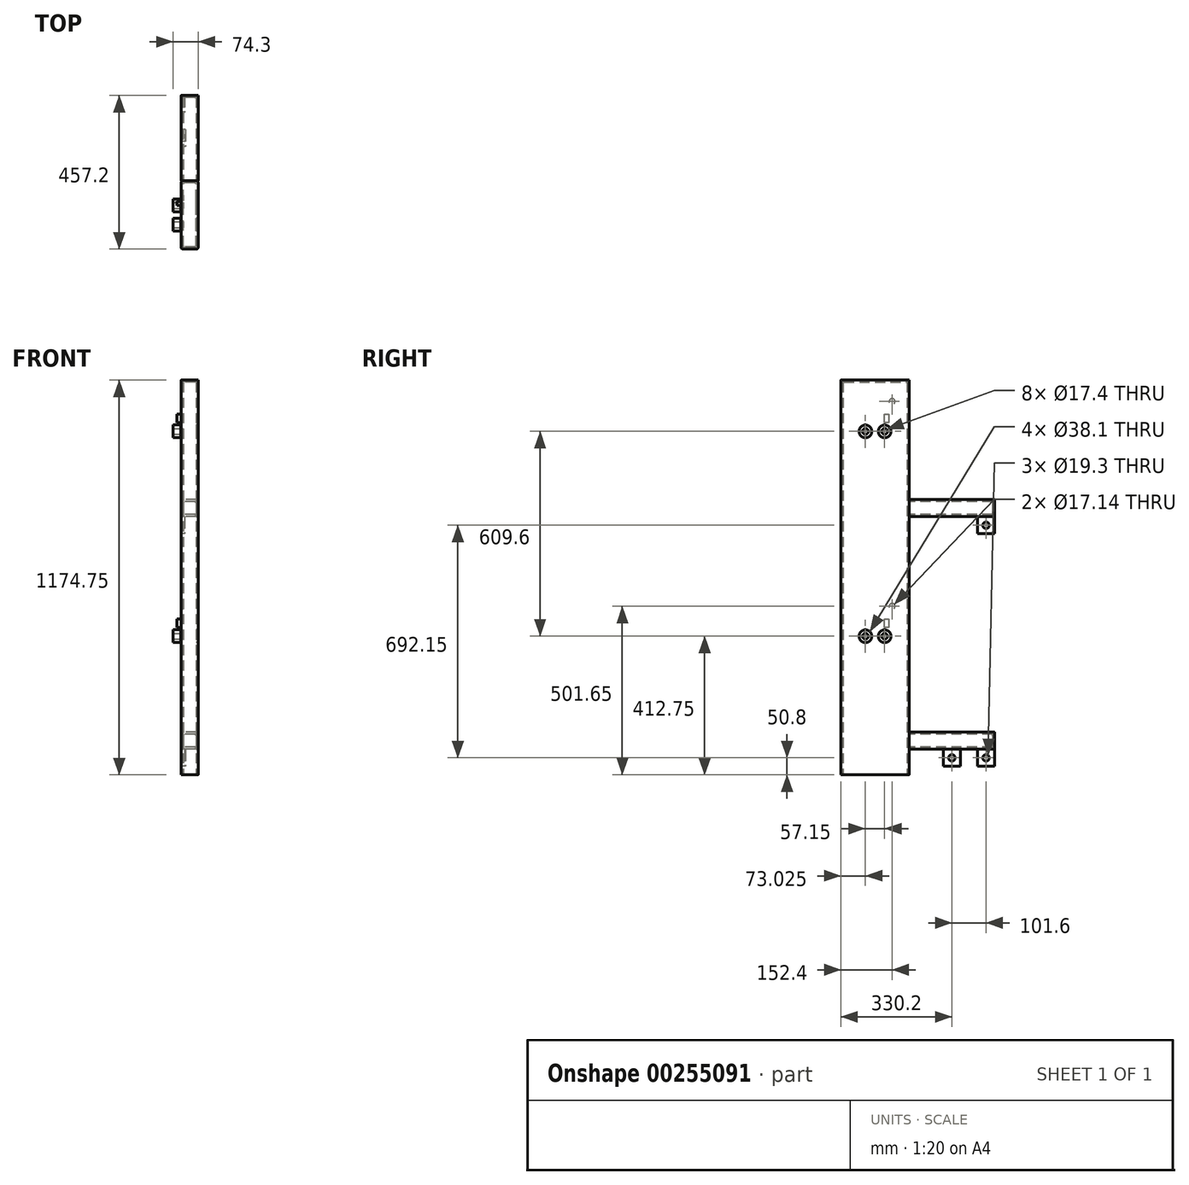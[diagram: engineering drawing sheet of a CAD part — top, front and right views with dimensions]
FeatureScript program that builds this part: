
annotation { "Feature Type Name" : "Feature", "Feature Type Description" : "" }
export const myFeature = defineFeature(function(context is Context, id is Id, definition is map)
    precondition{}
    {
        {
            var Q0;
            Q0=qCreatedBy(makeId("Top.planeOp"),FACE);
            var sketch = newSketch(context, id + "F0", { "sketchPlane" : qUnion([Q0])});
            skLineSegment(sketch, "E0.bottom", {"start": v(19.43, -101.6) * mm, "end": v(-19.43, -101.6) * mm});
            skLineSegment(sketch, "E0.top", {"start": v(19.43, 101.6) * mm, "end": v(-19.43, 101.6) * mm});
            skLineSegment(sketch, "E0.left", {"start": v(25.4, -95.63) * mm, "end": v(25.4, 95.63) * mm});
            skLineSegment(sketch, "E0.right", {"start": v(-25.4, -95.63) * mm, "end": v(-25.4, 95.63) * mm});
            skPoint(sketch, "E0.middle", {"position": v(0, 0) * mm});
            skLineSegment(sketch, "E1.0", {"start": v(-19.05, -92.08) * mm, "end": v(-19.05, 92.08) * mm});
            skLineSegment(sketch, "E1.1", {"start": v(15.87, -95.25) * mm, "end": v(-15.88, -95.25) * mm});
            skLineSegment(sketch, "E1.2", {"start": v(19.05, -92.08) * mm, "end": v(19.05, 92.08) * mm});
            skLineSegment(sketch, "E1.3", {"start": v(15.88, 95.25) * mm, "end": v(-15.88, 95.25) * mm});
            skPoint(sketch, "E2.visualSharp", {"position": v(-19.05, 95.25) * mm});
            skArc(sketch, "E2.filletArc", {"start": v(-15.88, 95.25) * mm, "mid": v(-18.12, 94.32) * mm, "end": v(-19.05, 92.08) * mm});
            skPoint(sketch, "E3.visualSharp", {"position": v(19.05, 95.25) * mm});
            skArc(sketch, "E3.filletArc", {"start": v(19.05, 92.08) * mm, "mid": v(18.12, 94.32) * mm, "end": v(15.88, 95.25) * mm});
            skPoint(sketch, "E4.visualSharp", {"position": v(19.05, -95.25) * mm});
            skArc(sketch, "E4.filletArc", {"start": v(15.87, -95.25) * mm, "mid": v(18.12, -94.32) * mm, "end": v(19.05, -92.08) * mm});
            skPoint(sketch, "E5.visualSharp", {"position": v(-19.05, -95.25) * mm});
            skArc(sketch, "E5.filletArc", {"start": v(-19.05, -92.08) * mm, "mid": v(-18.12, -94.32) * mm, "end": v(-15.88, -95.25) * mm});
            skPoint(sketch, "E6.visualSharp", {"position": v(-25.4, 101.6) * mm});
            skArc(sketch, "E6.filletArc", {"start": v(-19.43, 101.6) * mm, "mid": v(-23.65, 99.85) * mm, "end": v(-25.4, 95.63) * mm});
            skPoint(sketch, "E7.visualSharp", {"position": v(25.4, 101.6) * mm});
            skArc(sketch, "E7.filletArc", {"start": v(25.4, 95.63) * mm, "mid": v(23.65, 99.85) * mm, "end": v(19.43, 101.6) * mm});
            skPoint(sketch, "E8.visualSharp", {"position": v(25.4, -101.6) * mm});
            skArc(sketch, "E8.filletArc", {"start": v(19.43, -101.6) * mm, "mid": v(23.65, -99.85) * mm, "end": v(25.4, -95.63) * mm});
            skPoint(sketch, "E9.visualSharp", {"position": v(-25.4, -101.6) * mm});
            skArc(sketch, "E9.filletArc", {"start": v(-25.4, -95.63) * mm, "mid": v(-23.65, -99.85) * mm, "end": v(-19.43, -101.6) * mm});
            skSolve(sketch);
        }
        {
            var Q0;
            Q0 = qSketchRegion(id + "F0", true);
            extrude(context, id + "F1", {"entities" : qUnion([Q0]), "depth" : 1168.4 * mm});
        }
        {
            var Q0;
            Q0=makeQuery(id+"F1.opExtrude","CAP_FACE",FACE,{"disambiguationData":[OSD([sQuery(id+"F0.wireOp",EDGE,"E0.bottom"),sQuery(id+"F0.wireOp",EDGE,"E0.top"),sQuery(id+"F0.wireOp",EDGE,"E0.left"),sQuery(id+"F0.wireOp",EDGE,"E0.right"),sQuery(id+"F0.wireOp",EDGE,"E1.0"),sQuery(id+"F0.wireOp",EDGE,"E1.1"),sQuery(id+"F0.wireOp",EDGE,"E1.2"),sQuery(id+"F0.wireOp",EDGE,"E1.3"),sQuery(id+"F0.wireOp",EDGE,"E2.filletArc"),sQuery(id+"F0.wireOp",EDGE,"E3.filletArc"),sQuery(id+"F0.wireOp",EDGE,"E4.filletArc"),sQuery(id+"F0.wireOp",EDGE,"E5.filletArc"),sQuery(id+"F0.wireOp",EDGE,"E6.filletArc"),sQuery(id+"F0.wireOp",EDGE,"E7.filletArc"),sQuery(id+"F0.wireOp",EDGE,"E8.filletArc"),sQuery(id+"F0.wireOp",EDGE,"E9.filletArc")])],"isStart":false});
            var sketch = newSketch(context, id + "F2", { "sketchPlane" : qUnion([Q0])});
            skArc(sketch, "E10.0", {"start": v(-19.43, 101.6) * mm, "mid": v(-23.65, 99.85) * mm, "end": v(-25.4, 95.63) * mm});
            skLineSegment(sketch, "E10.1", {"start": v(19.43, 101.6) * mm, "end": v(-19.43, 101.6) * mm});
            skArc(sketch, "E10.2", {"start": v(25.4, 95.63) * mm, "mid": v(23.65, 99.85) * mm, "end": v(19.43, 101.6) * mm});
            skLineSegment(sketch, "E10.3", {"start": v(25.4, -95.63) * mm, "end": v(25.4, 95.63) * mm});
            skLineSegment(sketch, "E10.4", {"start": v(-25.4, -95.63) * mm, "end": v(-25.4, 95.63) * mm});
            skArc(sketch, "E10.5", {"start": v(-25.4, -95.63) * mm, "mid": v(-23.65, -99.85) * mm, "end": v(-19.43, -101.6) * mm});
            skLineSegment(sketch, "E10.6", {"start": v(19.43, -101.6) * mm, "end": v(-19.43, -101.6) * mm});
            skArc(sketch, "E10.7", {"start": v(19.43, -101.6) * mm, "mid": v(23.65, -99.85) * mm, "end": v(25.4, -95.63) * mm});
            skSolve(sketch);
        }
        {
            var Q0;
            Q0 = qSketchRegion(id + "F2", true);
            extrude(context, id + "F3", {"entities" : qUnion([Q0]), "operationType" : NewBodyOperationType.ADD, "depth" : 6.35 * mm});
        }
        {
            var Q0;
            Q0=makeQuery(id+"F3.boolean.opBoolean","MERGE",FACE,{"derivedFrom":[makeQuery(id+"F1.opExtrude","SWEPT_FACE",FACE,{"disambiguationData":[OSD([sQuery(id+"F0.wireOp",EDGE,"E0.right")])]}),makeQuery(id+"F3.opExtrude","SWEPT_FACE",FACE,{"disambiguationData":[OSD([sQuery(id+"F2.wireOp",EDGE,"E10.4")])]})]});
            var sketch = newSketch(context, id + "F4", { "sketchPlane" : qUnion([Q0])});
            skLineSegment(sketch, "E11", {"start": v(-119.84, 1022.35) * mm, "end": v(114.78, 1022.35) * mm, "construction": true});
            skLineSegment(sketch, "E12", {"start": v(0, 1307.78) * mm, "end": v(0, -150.73) * mm, "construction": true});
            skPoint(sketch, "E13.orphan", {"position": v(0, 1174.75) * mm});
            skCircle(sketch, "E14", {"center": v(28.57, 1022.35) * mm, "radius": 19.05 * mm});
            skCircle(sketch, "E15", {"center": v(-28.58, 1022.35) * mm, "radius": 19.05 * mm});
            skCircle(sketch, "E16.0.1.0", {"center": v(-28.58, 412.75) * mm, "radius": 19.05 * mm});
            skCircle(sketch, "E16.0.1.1", {"center": v(28.57, 412.75) * mm, "radius": 19.05 * mm});
            skLineSegment(sketch, "E16.direction1", {"start": v(-28.58, 1022.35) * mm, "end": v(-3.18, 1022.35) * mm, "construction": true});
            skLineSegment(sketch, "E16.direction2", {"start": v(-28.58, 1022.35) * mm, "end": v(-28.58, 412.75) * mm, "construction": true});
            skSolve(sketch);
        }
        {
            var Q0;
            Q0 = qSketchRegion(id + "F4", true);
            extrude(context, id + "F5", {"entities" : qUnion([Q0]), "depth" : 23.5 * mm, "hasSecondDirection" : true, "secondDirectionOppositeDirection" : false, "secondDirectionDepth" : 1.27 * mm});
        }
        {
            var Q0;
            Q0=makeQuery(id+"F5.opExtrude","CAP_FACE",FACE,{"disambiguationData":[OSD([sQuery(id+"F4.wireOp",EDGE,"E14")])],"isStart":true});
            var sketch = newSketch(context, id + "F6", { "sketchPlane" : qUnion([Q0])});
            skCircle(sketch, "E17", {"center": v(-28.57, 1022.35) * mm, "radius": 7.94 * mm});
            skCircle(sketch, "E18", {"center": v(-28.57, 412.75) * mm, "radius": 7.94 * mm});
            skLineSegment(sketch, "E19", {"start": v(-28.57, 1075.13) * mm, "end": v(-28.57, 568.16) * mm, "construction": true});
            skSolve(sketch);
        }
        {
            var Q0;
            Q0 = qSketchRegion(id + "F6", true);
            extrude(context, id + "F7", {"entities" : qUnion([Q0]), "operationType" : NewBodyOperationType.ADD, "depth" : 38.1 * mm});
        }
        {
            var Q0;
            Q0=makeQuery(id+"F5.opExtrude","CAP_FACE",FACE,{"disambiguationData":[OSD([sQuery(id+"F4.wireOp",EDGE,"E15")])],"isStart":true});
            var sketch = newSketch(context, id + "F8", { "sketchPlane" : qUnion([Q0])});
            skCircle(sketch, "E20", {"center": v(28.58, 1022.35) * mm, "radius": 7.94 * mm});
            skLineSegment(sketch, "E21", {"start": v(28.58, 1064.46) * mm, "end": v(28.58, 607.48) * mm, "construction": true});
            skCircle(sketch, "E22", {"center": v(28.58, 412.75) * mm, "radius": 7.94 * mm});
            skSolve(sketch);
        }
        {
            var Q0;
            Q0 = qSketchRegion(id + "F8", true);
            extrude(context, id + "F9", {"entities" : qUnion([Q0]), "operationType" : NewBodyOperationType.ADD, "depth" : 38.1 * mm});
        }
        {
            var Q0;
            Q0=makeQuery(id+"F7.opExtrude","CAP_FACE",FACE,{"disambiguationData":[OSD([sQuery(id+"F6.wireOp",EDGE,"E17")])],"isStart":false});
            var sketch = newSketch(context, id + "F10", { "sketchPlane" : qUnion([Q0])});
            skCircle(sketch, "E23", {"center": v(-28.57, 1022.35) * mm, "radius": 19.05 * mm});
            skCircle(sketch, "E24", {"center": v(28.58, 1022.35) * mm, "radius": 19.05 * mm});
            skCircle(sketch, "E25.0.1.0", {"center": v(-28.57, 412.75) * mm, "radius": 19.05 * mm});
            skCircle(sketch, "E25.0.1.1", {"center": v(28.58, 412.75) * mm, "radius": 19.05 * mm});
            skLineSegment(sketch, "E25.direction1", {"start": v(-28.57, 1022.35) * mm, "end": v(-3.17, 1022.35) * mm, "construction": true});
            skLineSegment(sketch, "E25.direction2", {"start": v(-28.57, 1022.35) * mm, "end": v(-28.57, 412.75) * mm, "construction": true});
            skSolve(sketch);
        }
        {
            var Q0;
            Q0 = qSketchRegion(id + "F10", true);
            var Q1;
            Q1=makeQuery(id+"F3.boolean.opBoolean","MERGE",FACE,{"derivedFrom":[makeQuery(id+"F1.opExtrude","SWEPT_FACE",FACE,{"disambiguationData":[OSD([sQuery(id+"F0.wireOp",EDGE,"E0.left")])]}),makeQuery(id+"F3.opExtrude","SWEPT_FACE",FACE,{"disambiguationData":[OSD([sQuery(id+"F2.wireOp",EDGE,"E10.3")])]})]});
            extrude(context, id + "F11", {"entities" : qUnion([Q0]), "operationType" : NewBodyOperationType.REMOVE, "endBound" : BoundingType.UP_TO_SURFACE, "endBoundEntityFace" : qUnion([Q1]), "depth" : 25.4 * mm});
        }
        {
            var Q0;
            Q0=makeQuery(id+"F3.boolean.opBoolean","MERGE",FACE,{"derivedFrom":[makeQuery(id+"F1.opExtrude","SWEPT_FACE",FACE,{"disambiguationData":[OSD([sQuery(id+"F0.wireOp",EDGE,"E0.right")])]}),makeQuery(id+"F3.opExtrude","SWEPT_FACE",FACE,{"disambiguationData":[OSD([sQuery(id+"F2.wireOp",EDGE,"E10.4")])]})]});
            var sketch = newSketch(context, id + "F12", { "sketchPlane" : qUnion([Q0])});
            skLineSegment(sketch, "E26", {"start": v(-28.58, 1047.75) * mm, "end": v(-28.58, 1073.15) * mm});
            skLineSegment(sketch, "E27", {"start": v(-28.58, 1073.15) * mm, "end": v(-41.28, 1073.15) * mm});
            skLineSegment(sketch, "E28", {"start": v(-41.28, 1073.15) * mm, "end": v(-41.28, 1047.75) * mm});
            skLineSegment(sketch, "E29", {"start": v(-41.28, 1047.75) * mm, "end": v(-28.58, 1047.75) * mm});
            skLineSegment(sketch, "E30", {"start": v(-79.96, 1022.35) * mm, "end": v(86.7, 1022.35) * mm, "construction": true});
            skPoint(sketch, "E31", {"position": v(-28.58, 1022.35) * mm});
            skLineSegment(sketch, "E32.0.1.0", {"start": v(-41.28, 463.55) * mm, "end": v(-41.28, 438.15) * mm});
            skLineSegment(sketch, "E32.0.1.1", {"start": v(-28.58, 463.55) * mm, "end": v(-41.28, 463.55) * mm});
            skLineSegment(sketch, "E32.0.1.2", {"start": v(-28.58, 438.15) * mm, "end": v(-28.58, 463.55) * mm});
            skLineSegment(sketch, "E32.0.1.3", {"start": v(-41.28, 438.15) * mm, "end": v(-28.58, 438.15) * mm});
            skLineSegment(sketch, "E32.direction1", {"start": v(-41.28, 1047.75) * mm, "end": v(-15.88, 1047.75) * mm, "construction": true});
            skLineSegment(sketch, "E32.direction2", {"start": v(-41.28, 1047.75) * mm, "end": v(-41.28, 438.15) * mm, "construction": true});
            skSolve(sketch);
        }
        {
            var Q0;
            Q0 = qSketchRegion(id + "F12", true);
            extrude(context, id + "F13", {"entities" : qUnion([Q0]), "operationType" : NewBodyOperationType.ADD, "depth" : 12.7 * mm});
        }
        {
            var Q0;
            Q0=makeQuery(id+"F3.boolean.opBoolean","MERGE",FACE,{"derivedFrom":[makeQuery(id+"F1.opExtrude","SWEPT_FACE",FACE,{"disambiguationData":[OSD([sQuery(id+"F0.wireOp",EDGE,"E0.left")])]}),makeQuery(id+"F3.opExtrude","SWEPT_FACE",FACE,{"disambiguationData":[OSD([sQuery(id+"F2.wireOp",EDGE,"E10.3")])]})]});
            var sketch = newSketch(context, id + "F14", { "sketchPlane" : qUnion([Q0])});
            skCircle(sketch, "E33", {"center": v(-28.57, 1022.35) * mm, "radius": 8.7 * mm});
            skCircle(sketch, "E34", {"center": v(28.58, 1022.35) * mm, "radius": 8.7 * mm});
            skCircle(sketch, "E35.0.1.0", {"center": v(28.58, 412.75) * mm, "radius": 8.7 * mm});
            skCircle(sketch, "E35.0.1.1", {"center": v(-28.57, 412.75) * mm, "radius": 8.7 * mm});
            skLineSegment(sketch, "E35.direction1", {"start": v(-28.57, 1022.35) * mm, "end": v(-3.17, 1022.35) * mm, "construction": true});
            skLineSegment(sketch, "E35.direction2", {"start": v(-28.57, 1022.35) * mm, "end": v(-28.57, 412.75) * mm, "construction": true});
            skSolve(sketch);
        }
        {
            var Q0;
            Q0 = qSketchRegion(id + "F14", true);
            extrude(context, id + "F15", {"entities" : qUnion([Q0]), "operationType" : NewBodyOperationType.REMOVE, "endBound" : BoundingType.THROUGH_ALL, "oppositeDirection" : true, "depth" : 25.4 * mm});
        }
        {
            var Q0;
            Q0=makeQuery(id+"F3.boolean.opBoolean","MERGE",FACE,{"derivedFrom":[makeQuery(id+"F1.opExtrude","SWEPT_FACE",FACE,{"disambiguationData":[OSD([sQuery(id+"F0.wireOp",EDGE,"E0.top")])]}),makeQuery(id+"F3.opExtrude","SWEPT_FACE",FACE,{"disambiguationData":[OSD([sQuery(id+"F2.wireOp",EDGE,"E10.1")])]})]});
            var sketch = newSketch(context, id + "F16", { "sketchPlane" : qUnion([Q0])});
            skLineSegment(sketch, "E36.bottom", {"start": v(-19.43, 819.15) * mm, "end": v(19.43, 819.15) * mm});
            skLineSegment(sketch, "E36.top", {"start": v(-19.43, 768.35) * mm, "end": v(19.43, 768.35) * mm});
            skLineSegment(sketch, "E36.left", {"start": v(-25.4, 813.18) * mm, "end": v(-25.4, 774.32) * mm});
            skLineSegment(sketch, "E36.right", {"start": v(25.4, 813.18) * mm, "end": v(25.4, 774.32) * mm});
            skLineSegment(sketch, "E37.0", {"start": v(-15.88, 812.8) * mm, "end": v(15.88, 812.8) * mm});
            skLineSegment(sketch, "E37.1", {"start": v(-19.05, 809.63) * mm, "end": v(-19.05, 777.88) * mm});
            skLineSegment(sketch, "E37.2", {"start": v(-15.88, 774.7) * mm, "end": v(15.88, 774.7) * mm});
            skLineSegment(sketch, "E37.3", {"start": v(19.05, 809.63) * mm, "end": v(19.05, 777.88) * mm});
            skPoint(sketch, "E38.visualSharp", {"position": v(19.05, 812.8) * mm});
            skArc(sketch, "E38.filletArc", {"start": v(19.05, 809.63) * mm, "mid": v(18.12, 811.87) * mm, "end": v(15.88, 812.8) * mm});
            skPoint(sketch, "E39.visualSharp", {"position": v(19.05, 774.7) * mm});
            skArc(sketch, "E39.filletArc", {"start": v(15.88, 774.7) * mm, "mid": v(18.12, 775.63) * mm, "end": v(19.05, 777.88) * mm});
            skPoint(sketch, "E40.visualSharp", {"position": v(-19.05, 774.7) * mm});
            skArc(sketch, "E40.filletArc", {"start": v(-19.05, 777.88) * mm, "mid": v(-18.12, 775.63) * mm, "end": v(-15.88, 774.7) * mm});
            skPoint(sketch, "E41.visualSharp", {"position": v(-19.05, 812.8) * mm});
            skArc(sketch, "E41.filletArc", {"start": v(-15.88, 812.8) * mm, "mid": v(-18.12, 811.87) * mm, "end": v(-19.05, 809.63) * mm});
            skPoint(sketch, "E42.visualSharp", {"position": v(25.4, 819.15) * mm});
            skArc(sketch, "E42.filletArc", {"start": v(25.4, 813.18) * mm, "mid": v(23.65, 817.4) * mm, "end": v(19.43, 819.15) * mm});
            skPoint(sketch, "E43.visualSharp", {"position": v(25.4, 768.35) * mm});
            skArc(sketch, "E43.filletArc", {"start": v(19.43, 768.35) * mm, "mid": v(23.65, 770.1) * mm, "end": v(25.4, 774.32) * mm});
            skPoint(sketch, "E44.visualSharp", {"position": v(-25.4, 768.35) * mm});
            skArc(sketch, "E44.filletArc", {"start": v(-25.4, 774.32) * mm, "mid": v(-23.65, 770.1) * mm, "end": v(-19.43, 768.35) * mm});
            skPoint(sketch, "E45.visualSharp", {"position": v(-25.4, 819.15) * mm});
            skArc(sketch, "E45.filletArc", {"start": v(-19.43, 819.15) * mm, "mid": v(-23.65, 817.4) * mm, "end": v(-25.4, 813.18) * mm});
            skLineSegment(sketch, "E46.0.1.0", {"start": v(-19.05, 117.48) * mm, "end": v(-19.05, 85.73) * mm});
            skLineSegment(sketch, "E46.0.1.1", {"start": v(-25.4, 121.03) * mm, "end": v(-25.4, 82.17) * mm});
            skLineSegment(sketch, "E46.0.1.2", {"start": v(-15.88, 120.65) * mm, "end": v(15.88, 120.65) * mm});
            skLineSegment(sketch, "E46.0.1.3", {"start": v(19.05, 117.48) * mm, "end": v(19.05, 85.73) * mm});
            skLineSegment(sketch, "E46.0.1.4", {"start": v(-15.88, 82.55) * mm, "end": v(15.88, 82.55) * mm});
            skLineSegment(sketch, "E46.0.1.5", {"start": v(-19.43, 127) * mm, "end": v(19.43, 127) * mm});
            skLineSegment(sketch, "E46.0.1.6", {"start": v(25.4, 121.03) * mm, "end": v(25.4, 82.17) * mm});
            skLineSegment(sketch, "E46.0.1.7", {"start": v(-19.43, 76.2) * mm, "end": v(19.43, 76.2) * mm});
            skArc(sketch, "E46.0.1.8", {"start": v(19.43, 76.2) * mm, "mid": v(23.65, 77.95) * mm, "end": v(25.4, 82.17) * mm});
            skArc(sketch, "E46.0.1.9", {"start": v(-25.4, 82.17) * mm, "mid": v(-23.65, 77.95) * mm, "end": v(-19.43, 76.2) * mm});
            skArc(sketch, "E46.0.1.10", {"start": v(25.4, 121.03) * mm, "mid": v(23.65, 125.25) * mm, "end": v(19.43, 127) * mm});
            skArc(sketch, "E46.0.1.11", {"start": v(-19.43, 127) * mm, "mid": v(-23.65, 125.25) * mm, "end": v(-25.4, 121.03) * mm});
            skArc(sketch, "E46.0.1.12", {"start": v(-15.88, 120.65) * mm, "mid": v(-18.12, 119.72) * mm, "end": v(-19.05, 117.48) * mm});
            skArc(sketch, "E46.0.1.13", {"start": v(-19.05, 85.73) * mm, "mid": v(-18.12, 83.48) * mm, "end": v(-15.88, 82.55) * mm});
            skArc(sketch, "E46.0.1.14", {"start": v(15.88, 82.55) * mm, "mid": v(18.12, 83.48) * mm, "end": v(19.05, 85.73) * mm});
            skArc(sketch, "E46.0.1.15", {"start": v(19.05, 117.48) * mm, "mid": v(18.12, 119.72) * mm, "end": v(15.88, 120.65) * mm});
            skLineSegment(sketch, "E46.direction1", {"start": v(-19.43, 768.35) * mm, "end": v(5.97, 768.35) * mm, "construction": true});
            skLineSegment(sketch, "E46.direction2", {"start": v(-19.43, 768.35) * mm, "end": v(-19.43, 76.2) * mm, "construction": true});
            skSolve(sketch);
        }
        {
            var Q0;
            Q0 = qSketchRegion(id + "F16", true);
            extrude(context, id + "F17", {"entities" : qUnion([Q0]), "operationType" : NewBodyOperationType.ADD, "depth" : 247.65 * mm});
        }
        {
            var Q0;
            Q0=makeQuery(id+"F17.opExtrude","CAP_FACE",FACE,{"disambiguationData":[OSD([sQuery(id+"F16.wireOp",EDGE,"E36.bottom"),sQuery(id+"F16.wireOp",EDGE,"E36.top"),sQuery(id+"F16.wireOp",EDGE,"E36.left"),sQuery(id+"F16.wireOp",EDGE,"E36.right"),sQuery(id+"F16.wireOp",EDGE,"E37.0"),sQuery(id+"F16.wireOp",EDGE,"E37.1"),sQuery(id+"F16.wireOp",EDGE,"E37.2"),sQuery(id+"F16.wireOp",EDGE,"E37.3"),sQuery(id+"F16.wireOp",EDGE,"E38.filletArc"),sQuery(id+"F16.wireOp",EDGE,"E39.filletArc"),sQuery(id+"F16.wireOp",EDGE,"E40.filletArc"),sQuery(id+"F16.wireOp",EDGE,"E41.filletArc"),sQuery(id+"F16.wireOp",EDGE,"E42.filletArc"),sQuery(id+"F16.wireOp",EDGE,"E43.filletArc"),sQuery(id+"F16.wireOp",EDGE,"E44.filletArc"),sQuery(id+"F16.wireOp",EDGE,"E45.filletArc")])],"isStart":false});
            var sketch = newSketch(context, id + "F18", { "sketchPlane" : qUnion([Q0])});
            skLineSegment(sketch, "E47.0", {"start": v(-19.43, 819.15) * mm, "end": v(19.43, 819.15) * mm});
            skLineSegment(sketch, "E47.1", {"start": v(25.4, 813.18) * mm, "end": v(25.4, 774.32) * mm});
            skLineSegment(sketch, "E47.2", {"start": v(-19.43, 768.35) * mm, "end": v(19.43, 768.35) * mm});
            skLineSegment(sketch, "E47.3", {"start": v(-25.4, 813.18) * mm, "end": v(-25.4, 774.32) * mm});
            skArc(sketch, "E48.0", {"start": v(25.4, 813.18) * mm, "mid": v(23.65, 817.4) * mm, "end": v(19.43, 819.15) * mm});
            skArc(sketch, "E49.0", {"start": v(19.43, 768.35) * mm, "mid": v(23.65, 770.1) * mm, "end": v(25.4, 774.32) * mm});
            skArc(sketch, "E49.1", {"start": v(-25.4, 774.32) * mm, "mid": v(-23.65, 770.1) * mm, "end": v(-19.43, 768.35) * mm});
            skArc(sketch, "E49.2", {"start": v(-19.43, 819.15) * mm, "mid": v(-23.65, 817.4) * mm, "end": v(-25.4, 813.18) * mm});
            skSolve(sketch);
        }
        {
            var Q0;
            Q0 = qSketchRegion(id + "F18", true);
            extrude(context, id + "F19", {"entities" : qUnion([Q0]), "operationType" : NewBodyOperationType.ADD, "depth" : 6.35 * mm});
        }
        {
            var Q0;
            Q0=makeQuery(id+"F17.opExtrude","CAP_FACE",FACE,{"disambiguationData":[OSD([sQuery(id+"F16.wireOp",EDGE,"E46.0.1.0"),sQuery(id+"F16.wireOp",EDGE,"E46.0.1.1"),sQuery(id+"F16.wireOp",EDGE,"E46.0.1.2"),sQuery(id+"F16.wireOp",EDGE,"E46.0.1.3"),sQuery(id+"F16.wireOp",EDGE,"E46.0.1.4"),sQuery(id+"F16.wireOp",EDGE,"E46.0.1.5"),sQuery(id+"F16.wireOp",EDGE,"E46.0.1.6"),sQuery(id+"F16.wireOp",EDGE,"E46.0.1.7"),sQuery(id+"F16.wireOp",EDGE,"E46.0.1.8"),sQuery(id+"F16.wireOp",EDGE,"E46.0.1.9"),sQuery(id+"F16.wireOp",EDGE,"E46.0.1.10"),sQuery(id+"F16.wireOp",EDGE,"E46.0.1.11"),sQuery(id+"F16.wireOp",EDGE,"E46.0.1.12"),sQuery(id+"F16.wireOp",EDGE,"E46.0.1.13"),sQuery(id+"F16.wireOp",EDGE,"E46.0.1.14"),sQuery(id+"F16.wireOp",EDGE,"E46.0.1.15")])],"isStart":false});
            var sketch = newSketch(context, id + "F20", { "sketchPlane" : qUnion([Q0])});
            skLineSegment(sketch, "E50.0", {"start": v(-19.43, 127) * mm, "end": v(19.43, 127) * mm});
            skLineSegment(sketch, "E50.1", {"start": v(-25.4, 121.03) * mm, "end": v(-25.4, 82.17) * mm});
            skLineSegment(sketch, "E50.2", {"start": v(-19.43, 76.2) * mm, "end": v(19.43, 76.2) * mm});
            skLineSegment(sketch, "E50.3", {"start": v(25.4, 121.03) * mm, "end": v(25.4, 82.17) * mm});
            skArc(sketch, "E50.4", {"start": v(25.4, 121.03) * mm, "mid": v(23.65, 125.25) * mm, "end": v(19.43, 127) * mm});
            skArc(sketch, "E50.5", {"start": v(-19.43, 127) * mm, "mid": v(-23.65, 125.25) * mm, "end": v(-25.4, 121.03) * mm});
            skArc(sketch, "E50.6", {"start": v(-25.4, 82.17) * mm, "mid": v(-23.65, 77.95) * mm, "end": v(-19.43, 76.2) * mm});
            skArc(sketch, "E50.7", {"start": v(19.43, 76.2) * mm, "mid": v(23.65, 77.95) * mm, "end": v(25.4, 82.17) * mm});
            skSolve(sketch);
        }
        {
            var Q0;
            Q0 = qSketchRegion(id + "F20", true);
            extrude(context, id + "F21", {"entities" : qUnion([Q0]), "operationType" : NewBodyOperationType.ADD, "depth" : 6.35 * mm});
        }
        {
            var Q0;
            Q0=makeQuery(id+"F19.boolean.opBoolean","MERGE",FACE,{"derivedFrom":[makeQuery(id+"F17.opExtrude","SWEPT_FACE",FACE,{"disambiguationData":[OSD([sQuery(id+"F16.wireOp",EDGE,"E36.right")])]}),makeQuery(id+"F19.opExtrude","SWEPT_FACE",FACE,{"disambiguationData":[OSD([sQuery(id+"F18.wireOp",EDGE,"E47.1")])]})]});
            var sketch = newSketch(context, id + "F22", { "sketchPlane" : qUnion([Q0])});
            skLineSegment(sketch, "E51.bottom", {"start": v(-355.6, 768.35) * mm, "end": v(-355.6, 768.35) * mm});
            skLineSegment(sketch, "E51.top", {"start": v(-304.8, 717.55) * mm, "end": v(-355.6, 717.55) * mm});
            skLineSegment(sketch, "E51.left", {"start": v(-304.8, 768.35) * mm, "end": v(-304.8, 717.55) * mm});
            skLineSegment(sketch, "E51.right", {"start": v(-355.6, 768.35) * mm, "end": v(-355.6, 717.55) * mm});
            skCircle(sketch, "E52", {"center": v(-330.2, 742.95) * mm, "radius": 9.65 * mm});
            skPoint(sketch, "E52.centerSnap0", {"position": v(-330.2, 717.55) * mm});
            skLineSegment(sketch, "E53", {"start": v(-355.6, 768.35) * mm, "end": v(-304.8, 768.35) * mm});
            skLineSegment(sketch, "E54.0.1.0", {"start": v(-355.6, 76.2) * mm, "end": v(-304.8, 76.2) * mm});
            skLineSegment(sketch, "E54.0.1.1", {"start": v(-304.8, 76.2) * mm, "end": v(-304.8, 25.4) * mm});
            skLineSegment(sketch, "E54.0.1.2", {"start": v(-304.8, 25.4) * mm, "end": v(-355.6, 25.4) * mm});
            skLineSegment(sketch, "E54.0.1.3", {"start": v(-355.6, 76.2) * mm, "end": v(-355.6, 25.4) * mm});
            skCircle(sketch, "E54.0.1.4", {"center": v(-330.2, 50.8) * mm, "radius": 9.65 * mm});
            skLineSegment(sketch, "E54.direction1", {"start": v(-355.6, 717.55) * mm, "end": v(-330.2, 717.55) * mm, "construction": true});
            skLineSegment(sketch, "E54.direction2", {"start": v(-355.6, 717.55) * mm, "end": v(-355.6, 25.4) * mm, "construction": true});
            skSolve(sketch);
        }
        {
            var Q0;
            Q0 = qSketchRegion(id + "F22", true);
            extrude(context, id + "F23", {"entities" : qUnion([Q0]), "operationType" : NewBodyOperationType.ADD, "oppositeDirection" : true, "depth" : 11.1 * mm});
        }
        {
            var Q0;
            Q0=makeQuery(id+"F3.boolean.opBoolean","MERGE",FACE,{"derivedFrom":[makeQuery(id+"F1.opExtrude","SWEPT_FACE",FACE,{"disambiguationData":[OSD([sQuery(id+"F0.wireOp",EDGE,"E0.right")])]}),makeQuery(id+"F3.opExtrude","SWEPT_FACE",FACE,{"disambiguationData":[OSD([sQuery(id+"F2.wireOp",EDGE,"E10.4")])]})]});
            var sketch = newSketch(context, id + "F24", { "sketchPlane" : qUnion([Q0])});
            skLineSegment(sketch, "E55", {"start": v(-307.5, 1111.25) * mm, "end": v(261.36, 1111.25) * mm, "construction": true});
            skCircle(sketch, "E56", {"center": v(-50.8, 1111.25) * mm, "radius": 8.57 * mm});
            skCircle(sketch, "E57.0.1.0", {"center": v(-50.8, 501.65) * mm, "radius": 8.57 * mm});
            skLineSegment(sketch, "E57.direction1", {"start": v(-50.8, 1111.25) * mm, "end": v(-25.4, 1111.25) * mm, "construction": true});
            skLineSegment(sketch, "E57.direction2", {"start": v(-50.8, 1111.25) * mm, "end": v(-50.8, 501.65) * mm, "construction": true});
            skLineSegment(sketch, "E58", {"start": v(28.57, 1022.35) * mm, "end": v(-28.58, 1022.35) * mm, "construction": true});
            skSolve(sketch);
        }
        {
            var Q0;
            Q0 = qSketchRegion(id + "F24", true);
            extrude(context, id + "F25", {"entities" : qUnion([Q0]), "operationType" : NewBodyOperationType.REMOVE, "oppositeDirection" : true, "depth" : 25.4 * mm});
        }
        {
            var Q0;
            Q0=makeQuery(id+"F23.opExtrude","CAP_FACE",FACE,{"disambiguationData":[OSD([sQuery(id+"F22.wireOp",EDGE,"E54.0.1.0"),sQuery(id+"F22.wireOp",EDGE,"E54.0.1.1"),sQuery(id+"F22.wireOp",EDGE,"E54.0.1.2"),sQuery(id+"F22.wireOp",EDGE,"E54.0.1.3"),sQuery(id+"F22.wireOp",EDGE,"E54.0.1.4")])],"isStart":true});
            var sketch = newSketch(context, id + "F26", { "sketchPlane" : qUnion([Q0])});
            skLineSegment(sketch, "E59.bottom", {"start": v(-254, 76.2) * mm, "end": v(-203.2, 76.2) * mm});
            skLineSegment(sketch, "E59.top", {"start": v(-254, 25.4) * mm, "end": v(-203.2, 25.4) * mm});
            skLineSegment(sketch, "E59.left", {"start": v(-254, 76.2) * mm, "end": v(-254, 25.4) * mm});
            skLineSegment(sketch, "E59.right", {"start": v(-203.2, 76.2) * mm, "end": v(-203.2, 25.4) * mm});
            skCircle(sketch, "E60", {"center": v(-228.6, 50.8) * mm, "radius": 9.65 * mm});
            skPoint(sketch, "E60.centerSnap0", {"position": v(-228.6, 76.2) * mm});
            skPoint(sketch, "E60.centerSnap1", {"position": v(-304.8, 50.8) * mm});
            skSolve(sketch);
        }
        {
            var Q0;
            Q0 = qSketchRegion(id + "F26", true);
            extrude(context, id + "F27", {"entities" : qUnion([Q0]), "operationType" : NewBodyOperationType.ADD, "oppositeDirection" : true, "depth" : 12.7 * mm});
        }
    });
